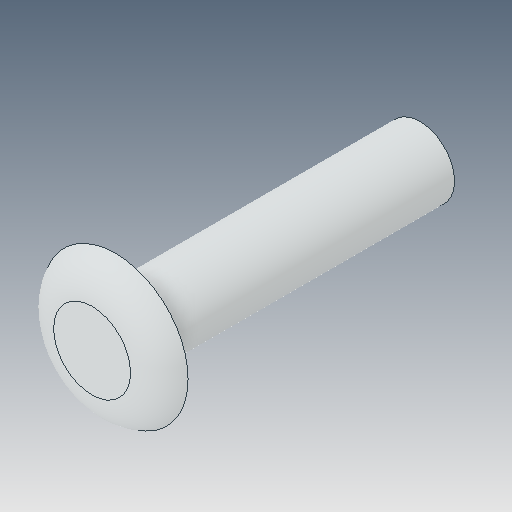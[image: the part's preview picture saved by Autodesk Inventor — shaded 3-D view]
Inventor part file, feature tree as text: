
AUTODESK INVENTOR PART (.ipt)
format: ipt  version: 2023.5 (Build 275446000, 446)  size: 103,424 bytes
history: native  units: in
note: dims shown in document units (in); Inventor stores cm internally (conversion verified against a paired STEP export)
features: fillet x1
ambient origin geometry x8: Origin, YZ Plane, XZ Plane, XY Plane, X Axis, Y Axis, Z Axis, Center Point
bodies: Solid1 (feature_tree)
feature tree (1):
  fillet  "Fillet1"  [1 undecoded]
note: 1 required parameter value undecoded (feature->parameter linkage not recoverable at this tier; creation-order binding heuristic only, values carry confidence <= 0.55)
